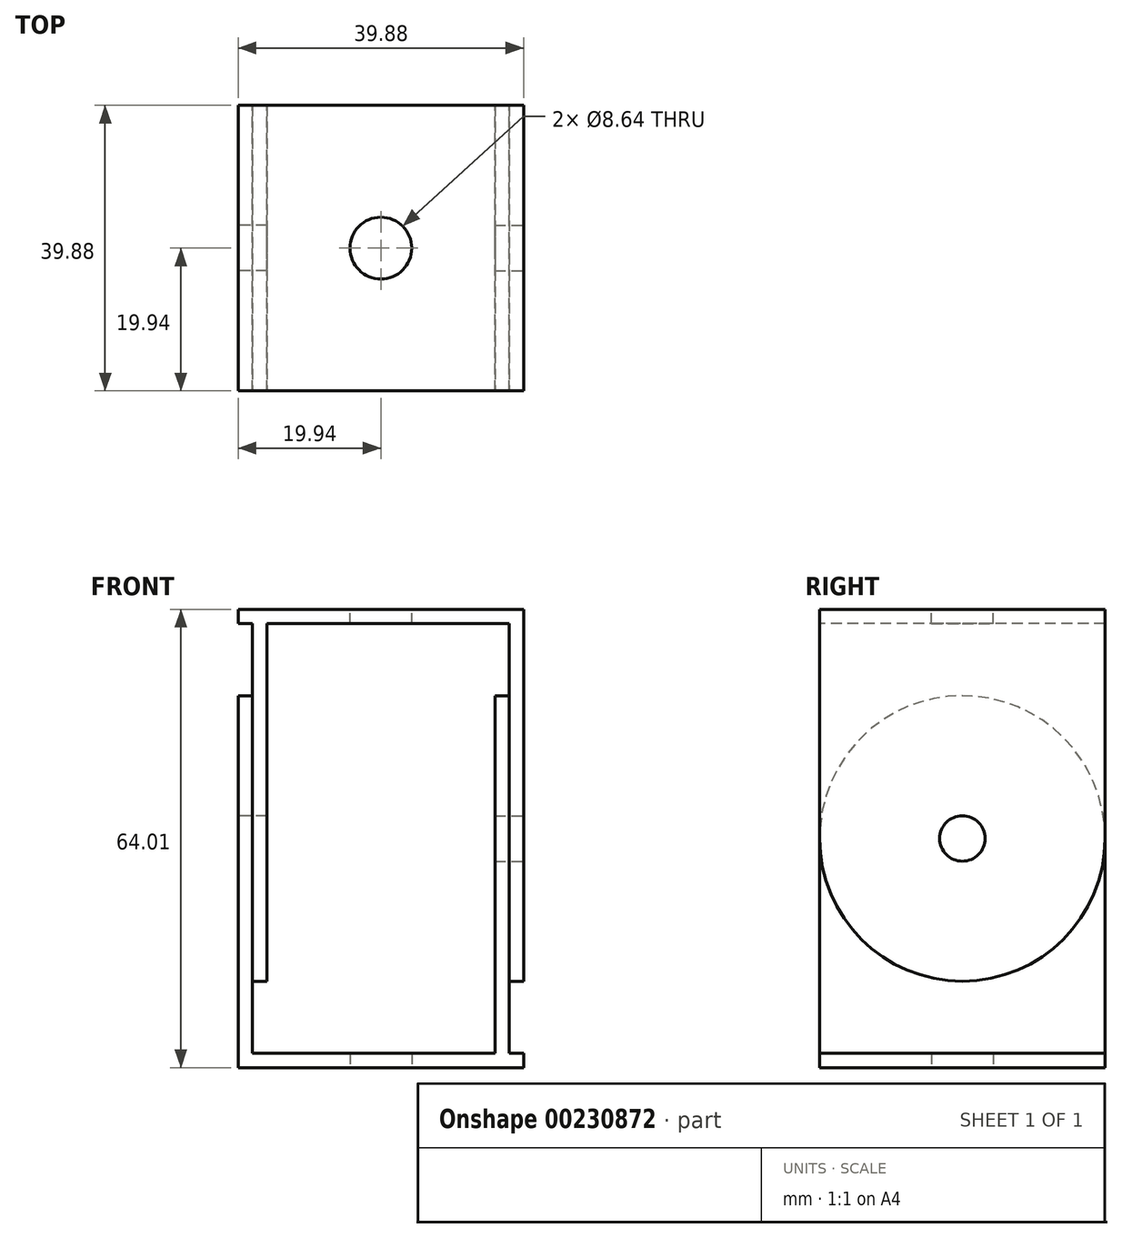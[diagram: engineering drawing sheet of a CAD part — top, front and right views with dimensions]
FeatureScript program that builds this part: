
annotation { "Feature Type Name" : "Feature", "Feature Type Description" : "" }
export const myFeature = defineFeature(function(context is Context, id is Id, definition is map)
    precondition{}
    {
        {
            var Q0;
            Q0=qCreatedBy(makeId("Top.planeOp"),FACE);
            var sketch = newSketch(context, id + "F0", { "sketchPlane" : qUnion([Q0])});
            skLineSegment(sketch, "E0.bottom", {"start": v(19.94, 19.94) * mm, "end": v(-19.94, 19.94) * mm});
            skLineSegment(sketch, "E0.top", {"start": v(19.94, -19.94) * mm, "end": v(-19.94, -19.94) * mm});
            skLineSegment(sketch, "E0.left", {"start": v(19.94, 19.94) * mm, "end": v(19.94, -19.94) * mm});
            skLineSegment(sketch, "E0.right", {"start": v(-19.94, 19.94) * mm, "end": v(-19.94, -19.94) * mm});
            skPoint(sketch, "E0.middle", {"position": v(0, 0) * mm});
            skCircle(sketch, "E1", {"center": v(0, 0) * mm, "radius": 4.32 * mm});
            skSolve(sketch);
        }
        {
            var Q0;
            Q0 = qSketchRegion(id + "F0", true);
            extrude(context, id + "F1", {"entities" : qUnion([Q0]), "depth" : 2 * mm});
        }
        {
            var Q0;
            Q0=qCreatedBy(makeId("Right.planeOp"),FACE);
            var sketch = newSketch(context, id + "F2", { "sketchPlane" : qUnion([Q0])});
            skLineSegment(sketch, "E2.0.0", {"start": v(-19.94, 0) * mm, "end": v(19.94, 0) * mm, "construction": true});
            skLineSegment(sketch, "E2.0.1", {"start": v(19.94, 0) * mm, "end": v(19.94, 2) * mm, "construction": true});
            skLineSegment(sketch, "E2.0.2", {"start": v(19.94, 2) * mm, "end": v(-19.94, 2) * mm, "construction": true});
            skLineSegment(sketch, "E2.0.3", {"start": v(-19.94, 2) * mm, "end": v(-19.94, 0) * mm, "construction": true});
            skLineSegment(sketch, "E3", {"start": v(-19.94, 32) * mm, "end": v(19.94, 32) * mm, "construction": true});
            skSolve(sketch);
        }
        {
            var Q0;
            Q0=qCreatedBy(makeId("Top.planeOp"),FACE);
            cPlane(context, id + "F3", {"entities" : qUnion([Q0]), "cplaneType" : CPlaneType.OFFSET, "offset" : 32 * mm, "width" : 152.4 * mm, "height" : 152.4 * mm});
        }
        {
            var Q0;
            Q0=makeQuery(id+"F1.opExtrude","SWEPT_BODY",BODY,{"disambiguationData":[OSD([sQuery(id+"F0.wireOp",EDGE,"E0.bottom"),sQuery(id+"F0.wireOp",EDGE,"E0.top"),sQuery(id+"F0.wireOp",EDGE,"E0.left"),sQuery(id+"F0.wireOp",EDGE,"E0.right"),sQuery(id+"F0.wireOp",EDGE,"E1")])]});
            var Q1;
            Q1=qCreatedBy(id+"F3.planeOp",FACE);
            mirror(context, id + "F4", {"entities" : qUnion([Q0]), "mirrorPlane" : qUnion([Q1])});
        }
        {
            var Q0;
            Q0=makeQuery(id+"F4.opPattern","COPY",FACE,{"derivedFrom":makeQuery(id+"F1.opExtrude","SWEPT_FACE",FACE,{"disambiguationData":[OSD([sQuery(id+"F0.wireOp",EDGE,"E0.left")])]}),"instanceName":"1"});
            var sketch = newSketch(context, id + "F5", { "sketchPlane" : qUnion([Q0])});
            skPoint(sketch, "E4.0", {"position": v(0, 32) * mm});
            skCircle(sketch, "E5", {"center": v(0, 32) * mm, "radius": 3.18 * mm});
            skArc(sketch, "E6", {"start": v(-19.94, 32) * mm, "mid": v(0, 12.06) * mm, "end": v(19.94, 32) * mm});
            skLineSegment(sketch, "E7", {"start": v(-19.94, 62) * mm, "end": v(-19.94, 32) * mm});
            skLineSegment(sketch, "E8", {"start": v(19.94, 62) * mm, "end": v(19.94, 32) * mm});
            skLineSegment(sketch, "E9", {"start": v(19.94, 62) * mm, "end": v(-19.94, 62) * mm});
            skSolve(sketch);
        }
        {
            var Q0;
            Q0 = qSketchRegion(id + "F5", true);
            extrude(context, id + "F6", {"entities" : qUnion([Q0]), "operationType" : NewBodyOperationType.ADD, "oppositeDirection" : true, "depth" : 2 * mm});
        }
        {
            var Q0;
            Q0=makeQuery(id+"F6.opExtrude","CAP_FACE",FACE,{"disambiguationData":[OSD([sQuery(id+"F5.wireOp",EDGE,"E5"),sQuery(id+"F5.wireOp",EDGE,"E6"),sQuery(id+"F5.wireOp",EDGE,"E7"),sQuery(id+"F5.wireOp",EDGE,"E8"),sQuery(id+"F5.wireOp",EDGE,"E9")])],"isStart":false});
            var sketch = newSketch(context, id + "F7", { "sketchPlane" : qUnion([Q0])});
            skCircle(sketch, "E10.0", {"center": v(0, 32) * mm, "radius": 3.18 * mm});
            skPoint(sketch, "E11.0", {"position": v(-19.94, 62) * mm});
            skPoint(sketch, "E12.0", {"position": v(19.94, 62) * mm});
            skPoint(sketch, "E13.0", {"position": v(-19.94, 2) * mm});
            skPoint(sketch, "E14.0", {"position": v(19.94, 2) * mm});
            skLineSegment(sketch, "E15", {"start": v(-19.94, 2) * mm, "end": v(-19.94, 32) * mm});
            skLineSegment(sketch, "E16", {"start": v(19.94, 32) * mm, "end": v(19.94, 2) * mm});
            skArc(sketch, "E17", {"start": v(19.94, 32) * mm, "mid": v(0, 51.94) * mm, "end": v(-19.94, 32) * mm});
            skLineSegment(sketch, "E18", {"start": v(-19.94, 2) * mm, "end": v(19.94, 2) * mm});
            skSolve(sketch);
        }
        {
            var Q0;
            Q0 = qSketchRegion(id + "F7", true);
            extrude(context, id + "F8", {"entities" : qUnion([Q0]), "operationType" : NewBodyOperationType.ADD, "depth" : 2 * mm});
        }
        {
            var Q0;
            Q0=makeQuery(id+"F1.opExtrude","SWEPT_FACE",FACE,{"disambiguationData":[OSD([sQuery(id+"F0.wireOp",EDGE,"E0.right")])]});
            var sketch = newSketch(context, id + "F9", { "sketchPlane" : qUnion([Q0])});
            skLineSegment(sketch, "E19.0.0", {"start": v(19.94, 2) * mm, "end": v(19.94, 32) * mm});
            skArc(sketch, "E19.0.1", {"start": v(19.94, 32) * mm, "mid": v(0, 51.94) * mm, "end": v(-19.94, 32) * mm});
            skLineSegment(sketch, "E19.0.2", {"start": v(-19.94, 32) * mm, "end": v(-19.94, 2) * mm});
            skLineSegment(sketch, "E19.0.3", {"start": v(-19.94, 2) * mm, "end": v(19.94, 2) * mm});
            skCircle(sketch, "E20.0", {"center": v(0, 32) * mm, "radius": 3.18 * mm});
            skSolve(sketch);
        }
        {
            var Q0;
            Q0 = qSketchRegion(id + "F9", true);
            extrude(context, id + "F10", {"entities" : qUnion([Q0]), "operationType" : NewBodyOperationType.ADD, "oppositeDirection" : true, "depth" : 2 * mm});
        }
        {
            var Q0;
            Q0=makeQuery(id+"F10.opExtrude","CAP_FACE",FACE,{"disambiguationData":[OSD([sQuery(id+"F9.wireOp",EDGE,"E19.0.0"),sQuery(id+"F9.wireOp",EDGE,"E19.0.1"),sQuery(id+"F9.wireOp",EDGE,"E19.0.2"),sQuery(id+"F9.wireOp",EDGE,"E19.0.3"),sQuery(id+"F9.wireOp",EDGE,"E20.0")])],"isStart":false});
            var sketch = newSketch(context, id + "F11", { "sketchPlane" : qUnion([Q0])});
            skLineSegment(sketch, "E21.0.0", {"start": v(19.94, 64) * mm, "end": v(-19.94, 64) * mm});
            skLineSegment(sketch, "E21.0.1", {"start": v(-19.94, 64) * mm, "end": v(-19.94, 32) * mm});
            skArc(sketch, "E21.0.2", {"start": v(-19.94, 32) * mm, "mid": v(0, 12.06) * mm, "end": v(19.94, 32) * mm});
            skLineSegment(sketch, "E21.0.3", {"start": v(19.94, 32) * mm, "end": v(19.94, 64) * mm});
            skCircle(sketch, "E22.0", {"center": v(0, 32) * mm, "radius": 3.18 * mm});
            skSolve(sketch);
        }
        {
            var Q0;
            Q0 = qSketchRegion(id + "F11", true);
            extrude(context, id + "F12", {"entities" : qUnion([Q0]), "operationType" : NewBodyOperationType.ADD, "depth" : 2 * mm});
        }
        {
            var Q0;
            Q0=makeQuery(id+"F10.boolean.opBoolean","MERGE",FACE,{"derivedFrom":[makeQuery(id+"F1.opExtrude","SWEPT_FACE",FACE,{"disambiguationData":[OSD([sQuery(id+"F0.wireOp",EDGE,"E0.right")])]}),makeQuery(id+"F10.opExtrude","CAP_FACE",FACE,{"disambiguationData":[OSD([sQuery(id+"F9.wireOp",EDGE,"E19.0.0"),sQuery(id+"F9.wireOp",EDGE,"E19.0.1"),sQuery(id+"F9.wireOp",EDGE,"E19.0.2"),sQuery(id+"F9.wireOp",EDGE,"E19.0.3"),sQuery(id+"F9.wireOp",EDGE,"E20.0")])],"isStart":true})]});
            var sketch = newSketch(context, id + "F13", { "sketchPlane" : qUnion([Q0])});
            skCircle(sketch, "E23.0", {"center": v(0, 32) * mm, "radius": 3.18 * mm});
            skSolve(sketch);
        }
        {
            var Q0;
            Q0 = qSketchRegion(id + "F13", true);
            var Q1;
            Q1=makeQuery(id+"F12.opExtrude","CAP_FACE",FACE,{"disambiguationData":[OSD([sQuery(id+"F11.wireOp",EDGE,"E21.0.0"),sQuery(id+"F11.wireOp",EDGE,"E21.0.1"),sQuery(id+"F11.wireOp",EDGE,"E21.0.2"),sQuery(id+"F11.wireOp",EDGE,"E21.0.3"),sQuery(id+"F11.wireOp",EDGE,"E22.0")])],"isStart":false});
            extrude(context, id + "F14", {"entities" : qUnion([Q0]), "endBound" : BoundingType.UP_TO_SURFACE, "oppositeDirection" : true, "endBoundEntityFace" : qUnion([Q1]), "depth" : 25.4 * mm});
        }
        {
            var Q0;
            Q0=makeQuery(id+"F14.opExtrude","SWEPT_BODY",BODY,{"disambiguationData":[OSD([sQuery(id+"F13.wireOp",EDGE,"E23.0")])]});
            var Q1;
            Q1=qCreatedBy(makeId("Right.planeOp"),FACE);
            mirror(context, id + "F15", {"entities" : qUnion([Q0]), "mirrorPlane" : qUnion([Q1])});
        }
    });
